# Revit family: Assa Abloy SL500 EXR-SL_R20
name_source: partatom
category: Doors
units: mm (PartAtom-declared; Revit-internal decimal feet)

## family parameters
Always vertical = Yes
Cut with Voids When Loaded = No
Host = Wall
OmniClass Number = 23.30.10.00
OmniClass Title = Doors
Room Calculation Point = No
Shared = No

## types (2) — shared parameters
Analytic Construction = <None>
Ctrl 2D Work Offset = 0"
Ctrl Pass Thru Work Offset = 0"
Ctrl Work Offset Main Door = 1 1/2"
Define Thermal Properties by = Schematic Type
Description = Standard and Impact doors with Dry Glazing
Door Bottom Stile Height = 10"
Door Mid Stile Height = 4"
Door Mid Stile Top = 38"
Door Thickness = 1 3/4"
Door Width = 23 11/16"
Door Width Between 96" to 120" = 96"
Fire Rating = 0 Hour
Frame Depth = 4 1/2"
Frame Thickness = 1 3/4"
Function = Exterior
Glass Stops = 1 1/4"
Header Cover = 9"
Height = 92"
Height R.O. = 1/4"
IFC Classification = Door
Manufacturer = ASSA ABLOY Entrance Systems
Masterformat 2014 Code = 08 42 29.23
Masterformat 2014 Description = Sliding Automatic Entrances
Maximium Opening = 30"
Model = SL500 EXR-SL
NBS Reference Code = 25-30-20-77
NBS Reference Description = Sliding Doorset Systems
OmniClass Code = 23-13 33 21 11 11
OmniClass Description = Automatic Aluminum-Framed Entrances
Automatic Aluminum-Framed Entrances
Automatic Aluminum-Framed Entrances
Operation = Exterior Entrance Door
Pass Through Door Width = 22 5/16"
Product Group = Overhead Concealed
Rough Height = 92 1/4"
Rough Width = 96 1/2"
STD CDO = 82"
Service Opening Height = 32 3/4"
Side Mullion Width = 2 5/8"
Thickness = 1 3/4"
URL = http://www.assaabloyentrance.com
Uniclass 1.4 Code = Sliding
Uniclass 1.4 Description = L4133
Uniclass 2.0 Code = Sliding Doorset Systems
Uniclass 2.0 Description = SS-25-30-20-77
Version = 1.0
Wall Closure = By host
Width = 96"
Width R.O. = 1/4"
Width_Max = 120"
Width_Min = 96"

## per-type parameters (varying)
| type | Door Glazing Thickness |
| Impact Door 8'-0" x 7'-8" (9/16" Glass) | 9/16" |
| Standard Door 8'-0" x 7'-8" (1/4" Glass) | 1/4" |

## geometry (parser evidence)
native form markers: Sweep x5
no freeform markers — native parametric forms only
